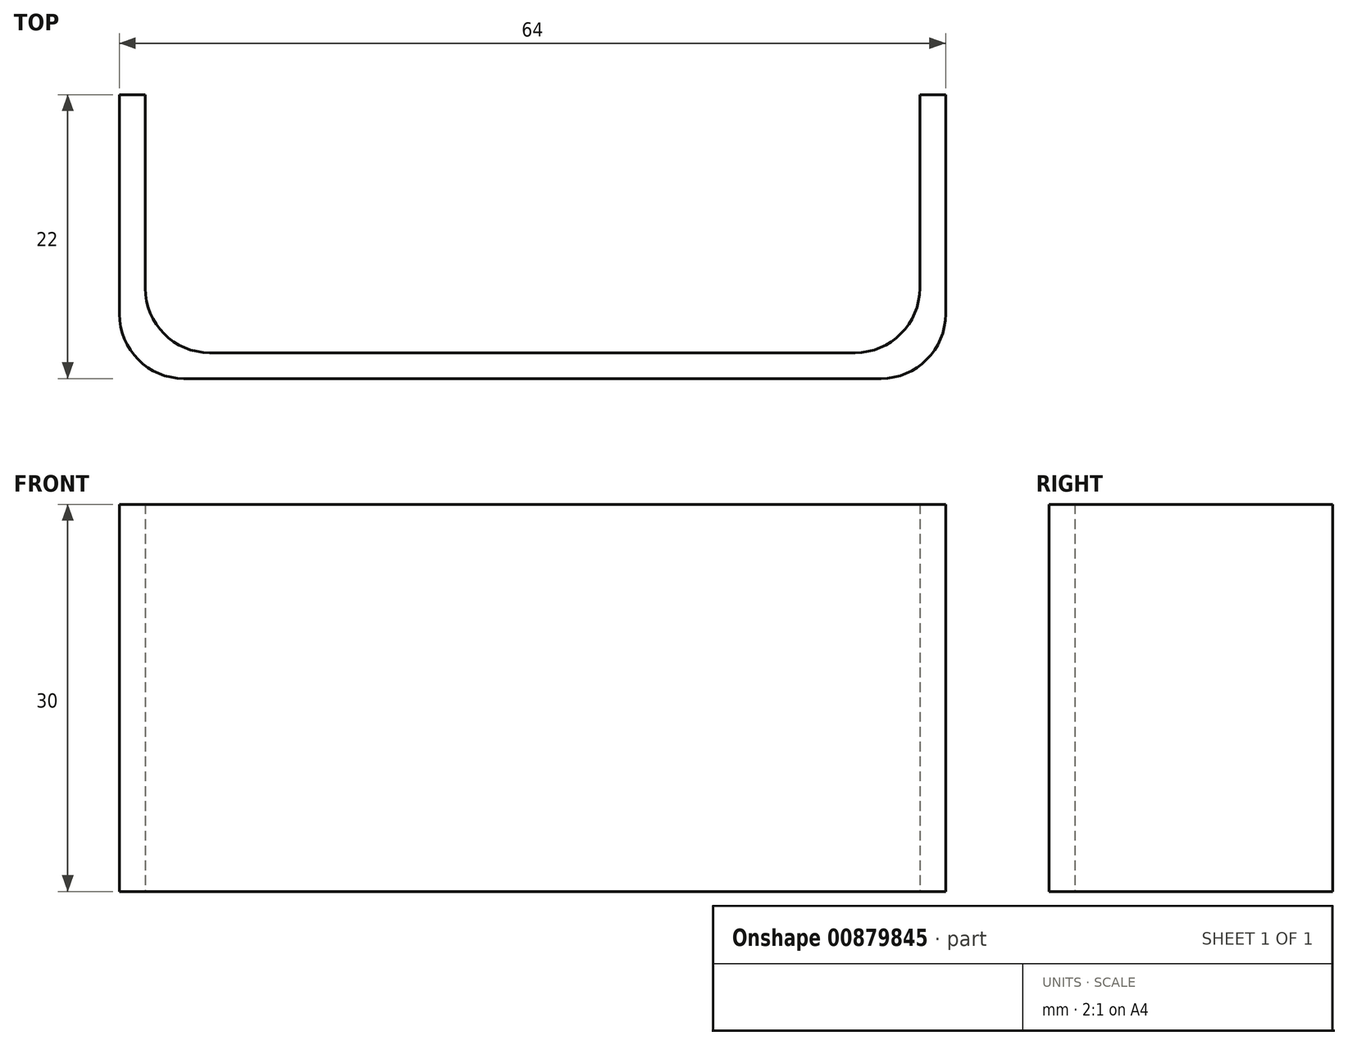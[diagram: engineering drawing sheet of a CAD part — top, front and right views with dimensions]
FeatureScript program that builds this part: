
annotation { "Feature Type Name" : "Feature", "Feature Type Description" : "" }
export const myFeature = defineFeature(function(context is Context, id is Id, definition is map)
    precondition{}
    {
        {
            var Q0;
            Q0=qCreatedBy(makeId("Top.planeOp"),FACE);
            var sketch = newSketch(context, id + "F0", { "sketchPlane" : qUnion([Q0])});
            skLineSegment(sketch, "E0", {"start": v(0, 0) * mm, "end": v(25, 0) * mm});
            skLineSegment(sketch, "E1", {"start": v(30, 5) * mm, "end": v(30, 20) * mm});
            skLineSegment(sketch, "E2", {"start": v(30, 20) * mm, "end": v(32, 20) * mm});
            skLineSegment(sketch, "E3", {"start": v(32, 20) * mm, "end": v(32, 3) * mm});
            skLineSegment(sketch, "E4", {"start": v(27, -2) * mm, "end": v(0, -2) * mm});
            skPoint(sketch, "E5.visualSharp", {"position": v(30, 0) * mm});
            skArc(sketch, "E5.filletArc", {"start": v(25, 0) * mm, "mid": v(28.54, 1.46) * mm, "end": v(30, 5) * mm});
            skPoint(sketch, "E6.visualSharp", {"position": v(32, -2) * mm});
            skArc(sketch, "E6.filletArc", {"start": v(27, -2) * mm, "mid": v(30.54, -0.54) * mm, "end": v(32, 3) * mm});
            skLineSegment(sketch, "E7.MirrorCS", {"start": v(-30, 20) * mm, "end": v(-32, 20) * mm});
            skArc(sketch, "E8.MirrorCS", {"start": v(-27, -2) * mm, "mid": v(-30.54, -0.54) * mm, "end": v(-32, 3) * mm});
            skArc(sketch, "E9.MirrorCS", {"start": v(-25, 0) * mm, "mid": v(-28.54, 1.46) * mm, "end": v(-30, 5) * mm});
            skPoint(sketch, "E10.MirrorP", {"position": v(-32, -2) * mm});
            skPoint(sketch, "E11.MirrorP", {"position": v(-30, 0) * mm});
            skLineSegment(sketch, "E12.MirrorCS", {"start": v(-30, 5) * mm, "end": v(-30, 20) * mm});
            skLineSegment(sketch, "E13.MirrorCS", {"start": v(-27, -2) * mm, "end": v(0, -2) * mm});
            skLineSegment(sketch, "E14.MirrorCS", {"start": v(-32, 20) * mm, "end": v(-32, 3) * mm});
            skLineSegment(sketch, "E15.MirrorCS", {"start": v(0, 0) * mm, "end": v(-25, 0) * mm});
            skSolve(sketch);
        }
        {
            var Q0;
            Q0=qSketchRegion(id+"F0",true);
            extrude(context, id + "F1", {"entities" : qUnion([Q0]), "depth" : 30 * mm, "offsetDistance" : 25 * mm});
        }
    });
